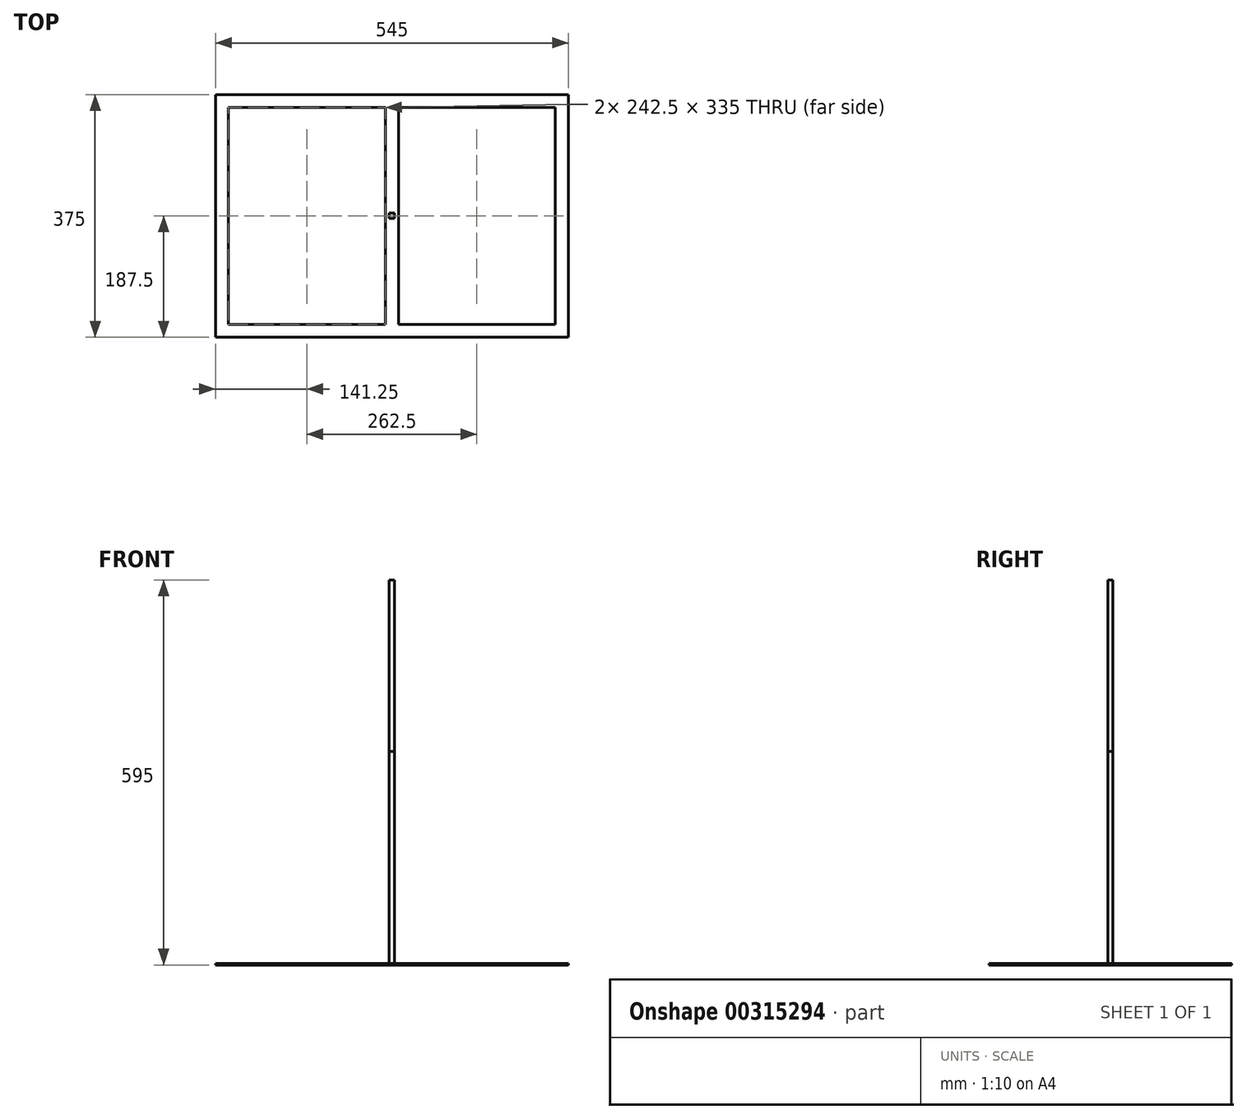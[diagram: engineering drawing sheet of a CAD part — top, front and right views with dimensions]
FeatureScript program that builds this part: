
annotation { "Feature Type Name" : "Feature", "Feature Type Description" : "" }
export const myFeature = defineFeature(function(context is Context, id is Id, definition is map)
    precondition{}
    {
        {
            var Q0;
            Q0=qCreatedBy(makeId("Top.planeOp"),FACE);
            var sketch = newSketch(context, id + "F0", { "sketchPlane" : qUnion([Q0])});
            skLineSegment(sketch, "E0.bottom", {"start": v(272.5, 187.5) * mm, "end": v(-272.5, 187.5) * mm});
            skLineSegment(sketch, "E0.top", {"start": v(272.5, -187.5) * mm, "end": v(-272.5, -187.5) * mm});
            skLineSegment(sketch, "E0.left", {"start": v(272.5, 187.5) * mm, "end": v(272.5, -187.5) * mm});
            skLineSegment(sketch, "E0.right", {"start": v(-272.5, 187.5) * mm, "end": v(-272.5, -187.5) * mm});
            skPoint(sketch, "E0.middle", {"position": v(0, 0) * mm});
            skLineSegment(sketch, "E1.0", {"start": v(252.5, -167.5) * mm, "end": v(-252.5, -167.5) * mm});
            skLineSegment(sketch, "E1.1", {"start": v(252.5, 167.5) * mm, "end": v(252.5, -167.5) * mm});
            skLineSegment(sketch, "E1.2", {"start": v(252.5, 167.5) * mm, "end": v(-252.5, 167.5) * mm});
            skLineSegment(sketch, "E1.3", {"start": v(-252.5, 167.5) * mm, "end": v(-252.5, -167.5) * mm});
            skLineSegment(sketch, "E2", {"start": v(0, 167.5) * mm, "end": v(0, -167.5) * mm, "construction": true});
            skLineSegment(sketch, "E3.0", {"start": v(-10, 167.5) * mm, "end": v(-10, -167.5) * mm});
            skLineSegment(sketch, "E4.MirrorCS", {"start": v(10, 167.5) * mm, "end": v(10, -167.5) * mm});
            skSolve(sketch);
        }
        {
            var Q0;
            Q0 = qSketchRegion(id + "F0", true);
            var Q1;
            {var subQ0=sQuery(id+"F0.wireOp",EDGE,"E3.0");Q1=makeQuery(id+"F0.imprint","IMPRINT",FACE,{"disambiguationData":[TD([[makeQuery(id+"F0.imprint","IMPRINT",EDGE,{"derivedFrom":subQ0}),1.0]])]});}
            extrude(context, id + "F1", {"entities" : qUnion([Q0, Q1]), "depth" : 2.5 * mm});
        }
        {
            var Q0;
            Q0=qCreatedBy(makeId("Top.planeOp"),FACE);
            var sketch = newSketch(context, id + "F2", { "sketchPlane" : qUnion([Q0])});
            skLineSegment(sketch, "E5.bottom", {"start": v(4, 4) * mm, "end": v(-4, 4) * mm});
            skLineSegment(sketch, "E5.top", {"start": v(4, -4) * mm, "end": v(-4, -4) * mm});
            skLineSegment(sketch, "E5.left", {"start": v(4, 4) * mm, "end": v(4, -4) * mm});
            skLineSegment(sketch, "E5.right", {"start": v(-4, 4) * mm, "end": v(-4, -4) * mm});
            skPoint(sketch, "E5.middle", {"position": v(0, 0) * mm});
            skSolve(sketch);
        }
        {
            var Q0;
            Q0 = qSketchRegion(id + "F2", true);
            extrude(context, id + "F3", {"entities" : qUnion([Q0]), "depth" : 330 * mm});
        }
        {
            var Q0;
            Q0=makeQuery(id+"F3.opExtrude","CAP_FACE",FACE,{"disambiguationData":[OSD([sQuery(id+"F2.wireOp",EDGE,"E5.bottom"),sQuery(id+"F2.wireOp",EDGE,"E5.top"),sQuery(id+"F2.wireOp",EDGE,"E5.left"),sQuery(id+"F2.wireOp",EDGE,"E5.right")])],"isStart":false});
            extrude(context, id + "F4", {"entities" : qUnion([Q0]), "depth" : 265 * mm});
        }
    });
